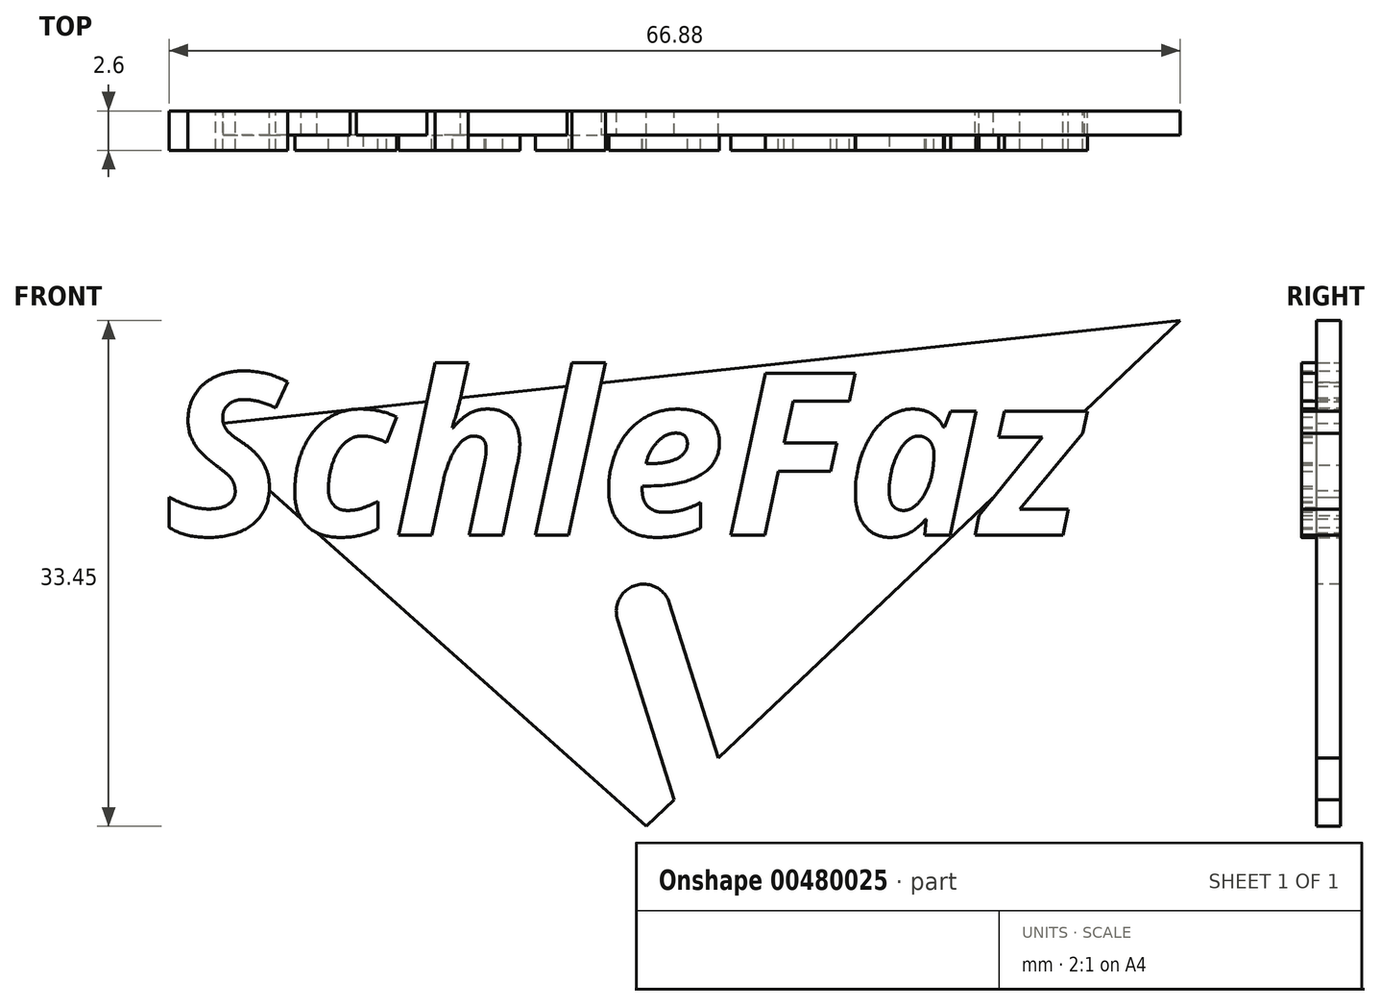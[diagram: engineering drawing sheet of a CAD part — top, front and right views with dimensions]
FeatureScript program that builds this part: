
annotation { "Feature Type Name" : "Feature", "Feature Type Description" : "" }
export const myFeature = defineFeature(function(context is Context, id is Id, definition is map)
    precondition{}
    {
        {
            var Q0;
            Q0=qCreatedBy(makeId("Front.planeOp"),FACE);
            var sketch = newSketch(context, id + "F0", { "sketchPlane" : qUnion([Q0])});
            skLineSegment(sketch, "E0", {"start": v(-25.42, 1.4) * mm, "end": v(4.24, -25.05) * mm});
            skLineSegment(sketch, "E1", {"start": v(4.24, -25.05) * mm, "end": v(39.58, 8.4) * mm});
            skLineSegment(sketch, "E2", {"start": v(39.58, 8.4) * mm, "end": v(-25.42, 1.4) * mm});
            skSolve(sketch);
        }
        {
            var Q0;
            Q0=makeQuery(id+"F0.imprint","IMPRINT",FACE,{"disambiguationData":[TD([[makeQuery(id+"F0.imprint","IMPRINT",EDGE,{"derivedFrom":sQuery(id+"F0.wireOp",EDGE,"E0")}),1.0]])]});
            extrude(context, id + "F1", {"entities" : qUnion([Q0]), "depth" : 1.6 * mm});
        }
        {
            var Q0;
            Q0=qCreatedBy(makeId("Front.planeOp"),FACE);
            var sketch = newSketch(context, id + "F2", { "sketchPlane" : qUnion([Q0])});
            skText(sketch, "E3", { "text": "SchleFaz", "fontName": "OpenSans-BoldItalic.ttf"});
            const initialGuessF2  = {"E3": [-0.0276, -0.0058, 1, 0, 0.0108]};
            skSetInitialGuess(sketch, initialGuessF2);
            skSolve(sketch);
        }
        {
            var Q0;
            Q0 = qSketchRegion(id + "F2", true);
            extrude(context, id + "F3", {"entities" : qUnion([Q0]), "operationType" : NewBodyOperationType.ADD, "depth" : 2.6 * mm});
        }
        {
            var Q0;
            Q0=qCreatedBy(makeId("Front.planeOp"),FACE);
            var sketch = newSketch(context, id + "F4", { "sketchPlane" : qUnion([Q0])});
            skLineSegment(sketch, "E4", {"start": v(6.3, -23.97) * mm, "end": v(2.35, -11.38) * mm});
            skLineSegment(sketch, "E5", {"start": v(9.74, -22.9) * mm, "end": v(5.79, -10.3) * mm});
            skLineSegment(sketch, "E6", {"start": v(2.35, -11.38) * mm, "end": v(5.79, -10.3) * mm, "construction": true});
            skArc(sketch, "E7", {"start": v(2.35, -11.38) * mm, "mid": v(3.53, -9.12) * mm, "end": v(5.79, -10.3) * mm});
            skLineSegment(sketch, "E8", {"start": v(6.3, -23.97) * mm, "end": v(9.74, -22.9) * mm});
            skSolve(sketch);
        }
        {
            var Q0;
            Q0=makeQuery(id+"F4.imprint","IMPRINT",FACE,{"disambiguationData":[TD([[makeQuery(id+"F4.imprint","IMPRINT",EDGE,{"derivedFrom":sQuery(id+"F4.wireOp",EDGE,"E4")}),-1.0]])]});
            extrude(context, id + "F5", {"entities" : qUnion([Q0]), "operationType" : NewBodyOperationType.REMOVE, "oppositeDirection" : true, "depth" : 25 * mm, "symmetric" : true});
        }
    });
